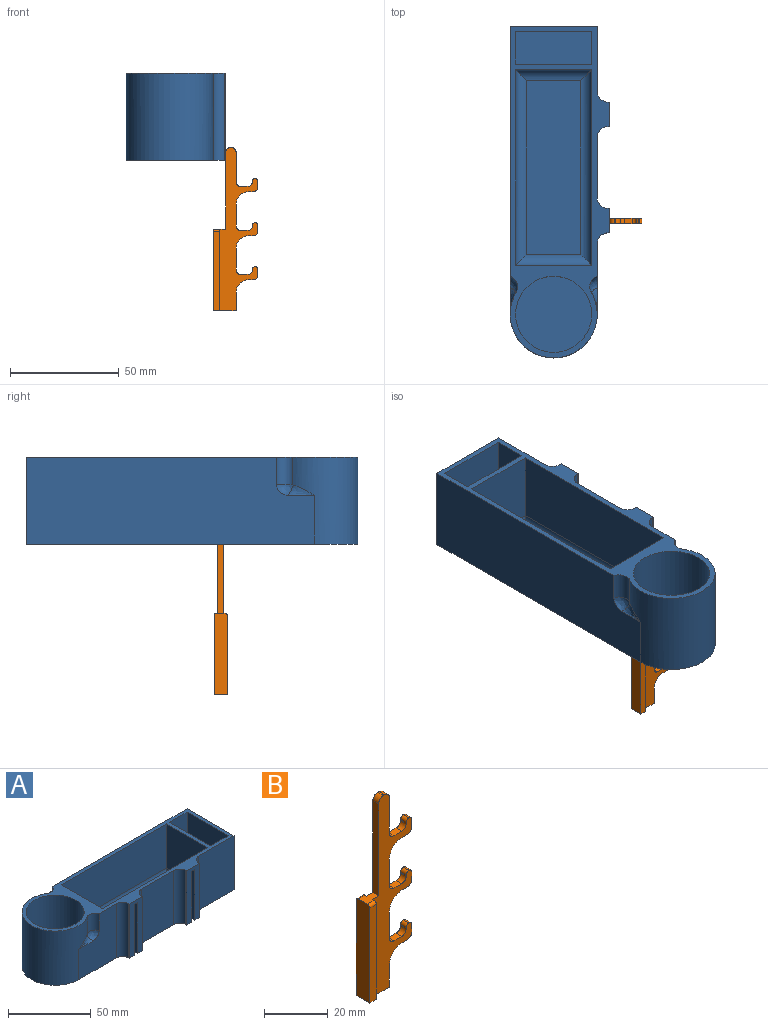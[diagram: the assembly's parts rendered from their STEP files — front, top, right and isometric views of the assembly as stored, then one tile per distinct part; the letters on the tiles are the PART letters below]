
ASSEMBLY  parts=2 mates=1
PART A: 56 faces, bbox 152.5x45.7x40 mm
  f0: plane 37.5x15mm, normal (0,1,0), area 562.5mm2, adj f1,f3,f4,f6
  f1: plane 37.5x35mm, normal (1,0,0), area 1312.5mm2, adj f0,f2,f4,f6
  f2: plane 37.5x15mm, normal (0,-1,0), area 562.5mm2, adj f1,f3,f4,f6
  f3: plane 37.5x35mm, normal (-1,0,0), area 1312.5mm2, adj f0,f2,f4,f6
  f4: plane 35x15mm, normal (0,0,1), area 525mm2, adj f0,f1,f2,f3
  f5: plane 6.2x5.7mm, normal (0,0,-1), area 26.6mm2, adj f9,f10,f11,f12,f13,f14,f15,f32
  f6: plane 152.5x45.7mm, normal (0,0,1), area 1382.2mm2, adj f0,f1,f2,f3,f23,f24,f25,f26
  f7: plane 6.2x5.7mm, normal (0,0,-1), area 26.6mm2, adj f16,f17,f18,f19,f20,f21,f22,f28
  f8: plane 152.5x45.7mm, normal (0,0,-1), area 6025mm2, adj f9,f10,f11,f12,f13,f14,f15,f16
  f9: plane 37.5x1.75mm, normal (0,1,0), area 65.6mm2, adj f5,f8,f10,f15
  f10: plane 37.5x3.2mm, normal (1,0,0), area 120mm2, adj f5,f8,f9,f11
  f11: plane 37.5x6.2mm, normal (0,-1,0), area 232.5mm2, adj f5,f8,f10,f12
  f12: plane 37.5x3.2mm, normal (-1,0,0), area 120mm2, adj f5,f8,f11,f13
  f13: plane 37.5x1.75mm, normal (0,1,0), area 65.6mm2, adj f5,f8,f12,f14
  f14: plane 37.5x2.5mm, normal (-1,0,0), area 93.8mm2, adj f5,f8,f13,f32
  f15: plane 37.5x2.5mm, normal (1,0,0), area 93.8mm2, adj f5,f8,f9,f32
  f16: plane 37.5x1.75mm, normal (0,1,0), area 65.6mm2, adj f7,f8,f17,f22
  f17: plane 37.5x3.2mm, normal (1,0,0), area 120mm2, adj f7,f8,f16,f18
  f18: plane 37.5x6.2mm, normal (0,-1,0), area 232.5mm2, adj f7,f8,f17,f19
  f19: plane 37.5x3.2mm, normal (-1,0,0), area 120mm2, adj f7,f8,f18,f20
  f20: plane 37.5x1.75mm, normal (0,1,0), area 65.6mm2, adj f7,f8,f19,f21
  f21: plane 37.5x2.5mm, normal (-1,0,0), area 93.8mm2, adj f7,f8,f20,f28
  f22: plane 37.5x2.5mm, normal (1,0,0), area 93.8mm2, adj f7,f8,f16,f28
  f23: cylinder r=20mm len=40mm, axis (0,0,1), area 2827.1mm2, adj f6,f8,f24,f34,f42,f43,f44,f45
  f24: plane 132.5x40mm, normal (0,1,0), area 4999.3mm2, adj f6,f8,f23,f25,f45,f46,f47
  f25: plane 40x40mm, normal (1,0,0), area 1600mm2, adj f6,f8,f24,f26
  f26: plane 40x29.89mm, normal (0,-1,0), area 1195.6mm2, adj f6,f8,f25,f48
  f27: plane 40x0.62mm, normal (1,0,0), area 24.8mm2, adj f6,f8,f28,f48
  f28: plane 40x11.2mm, normal (0,-1,0), area 346.8mm2, adj f6,f7,f8,f21,f22,f27,f29
  f29: plane 40x0.62mm, normal (-1,0,0), area 24.8mm2, adj f6,f8,f28,f51
  f30: plane 40x27.5mm, normal (0,-1,0), area 1100mm2, adj f6,f8,f50,f51
  f31: plane 40x0.62mm, normal (1,0,0), area 24.8mm2, adj f6,f8,f32,f50
  f32: plane 40x11.2mm, normal (0,-1,0), area 346.8mm2, adj f5,f6,f8,f14,f15,f31,f33
  f33: plane 40x0.62mm, normal (-1,0,0), area 24.8mm2, adj f6,f8,f32,f49
  f34: plane 40x32.39mm, normal (0,-1,0), area 994.9mm2, adj f6,f8,f23,f42,f43,f44,f49
  f35: plane 79.84x24.84mm, normal (0,0,1), area 1983.2mm2, adj f52,f53,f54,f55
  f36: plane 35x32.42mm, normal (1,0,0), area 1134.7mm2, adj f6,f37,f39,f54
  f37: plane 90x32.42mm, normal (0,1,0), area 2917.8mm2, adj f6,f36,f38,f55
  f38: plane 35x32.42mm, normal (-1,0,0), area 1134.7mm2, adj f6,f37,f39,f53
  f39: plane 90x32.42mm, normal (0,-1,0), area 2917.8mm2, adj f6,f36,f38,f52
  f40: plane 35x35mm, normal (0,0,1), area 962.1mm2, adj f41
  f41: cylinder r=17.5mm len=37.5mm, axis (0,0,-1), area 4123.3mm2, adj f6,f40
  f42: bspline ~13.08x4.89mm, area 33.2mm2, adj f23,f34,f43
  f43: bspline ~7.62x6.66mm, area 40.3mm2, adj f23,f34,f42,f44
  f44: cylinder r=5.08mm len=12.42mm, axis (0,0,1), area 111.9mm2, adj f6,f23,f34,f43
  f45: bspline ~13.08x4.89mm, area 33.7mm2, adj f23,f24,f46
  f46: bspline ~7.8x6.34mm, area 40.3mm2, adj f23,f24,f45,f47
  f47: cylinder r=5.08mm len=12.42mm, axis (0,0,1), area 111.9mm2, adj f6,f23,f24,f46
  f48: cylinder r=5.08mm len=40mm, axis (0,0,1), area 319.2mm2, adj f6,f8,f26,f27
  f49: cylinder r=5.08mm len=40mm, axis (0,0,1), area 319.2mm2, adj f6,f8,f33,f34
  f50: cylinder r=5.08mm len=40mm, axis (0,0,1), area 319.2mm2, adj f6,f8,f30,f31
  f51: cylinder r=5.08mm len=40mm, axis (0,0,-1), area 319.2mm2, adj f6,f8,f29,f30
  f52: cylinder r=5.08mm len=90mm, axis (1,0,0), area 688.7mm2, adj f35,f39,f53,f54
  f53: cylinder r=5.08mm len=35mm, axis (0,-1,0), area 249.8mm2, adj f35,f38,f52,f55
  f54: cylinder r=5.08mm len=35mm, axis (0,1,0), area 249.8mm2, adj f35,f36,f52,f55
  f55: cylinder r=5.08mm len=90mm, axis (-1,0,0), area 688.7mm2, adj f35,f37,f53,f54
PART B: 52 faces, bbox 20.5x6x75 mm
  f0: plane 2.5x0.51mm, normal (0,0,1), area 1.3mm2, adj f21,f22,f50,f51
  f1: plane 10.05x2.5mm, normal (1,0,0), area 25.1mm2, adj f21,f22,f25,f38
  f2: plane 2.5x2.3mm, normal (0,0,-1), area 5.7mm2, adj f21,f22,f27,f38
  f3: plane 2.84x2.5mm, normal (1,0,0), area 7.1mm2, adj f21,f22,f27,f33
  f4: plane 2.5x0.17mm, normal (0,0,1), area 0.4mm2, adj f21,f22,f32,f33
  f5: plane 2.5x0.34mm, normal (-1,0,0), area 0.8mm2, adj f21,f22,f26,f32
  f6: plane 3.5x2.5mm, normal (0,0,1), area 8.8mm2, adj f21,f22,f23,f26
  f7: plane 13.6x2.5mm, normal (1,0,0), area 34mm2, adj f21,f22,f23,f51
  f8: plane 10.5x6mm, normal (0,0,-1), area 36.8mm2, adj f9,f21,f22,f41,f42,f43,f44,f45
  f9: plane 8.55x2.5mm, normal (1,0,0), area 21.4mm2, adj f8,f21,f22,f39
  f10: plane 2.5x2.3mm, normal (0,0,-1), area 5.7mm2, adj f21,f22,f31,f39
  f11: plane 2.84x2.5mm, normal (1,0,0), area 7.1mm2, adj f21,f22,f31,f37
  f12: plane 2.5x0.17mm, normal (0,0,1), area 0.4mm2, adj f21,f22,f36,f37
  f13: plane 2.5x0.34mm, normal (-1,0,0), area 0.8mm2, adj f21,f22,f30,f36
  f14: plane 3.5x2.5mm, normal (0,0,1), area 8.8mm2, adj f21,f22,f24,f30
  f15: plane 10.05x2.5mm, normal (1,0,0), area 25.1mm2, adj f21,f22,f24,f40
  f16: plane 2.5x2.3mm, normal (0,0,-1), area 5.7mm2, adj f21,f22,f29,f40
  f17: plane 2.84x2.5mm, normal (1,0,0), area 7.1mm2, adj f21,f22,f29,f35
  f18: plane 2.5x0.17mm, normal (0,0,1), area 0.4mm2, adj f21,f22,f34,f35
  f19: plane 2.5x0.34mm, normal (-1,0,0), area 0.8mm2, adj f21,f22,f28,f34
  f20: plane 3.5x2.5mm, normal (0,0,1), area 8.8mm2, adj f21,f22,f25,f28
  f21: plane 75x17.5mm, normal (0,-1,0), area 582.3mm2, adj f0,f1,f2,f3,f4,f5,f6,f7
  f22: plane 75x17.5mm, normal (0,1,0), area 582.3mm2, adj f0,f1,f2,f3,f4,f5,f6,f7
  f23: cylinder r=2mm len=2.5mm, axis (0,1,0), area 7.9mm2, adj f6,f7,f21,f22
  f24: cylinder r=2mm len=2.5mm, axis (0,1,0), area 7.9mm2, adj f14,f15,f21,f22
  f25: cylinder r=2mm len=2.5mm, axis (0,1,0), area 7.9mm2, adj f1,f20,f21,f22
  f26: cylinder r=2mm len=2.5mm, axis (0,1,0), area 7.9mm2, adj f5,f6,f21,f22
  f27: cylinder r=2mm len=2.5mm, axis (0,1,0), area 7.9mm2, adj f2,f3,f21,f22
  f28: cylinder r=2mm len=2.5mm, axis (0,1,0), area 7.9mm2, adj f19,f20,f21,f22
  f29: cylinder r=2mm len=2.5mm, axis (0,1,0), area 7.9mm2, adj f16,f17,f21,f22
  f30: cylinder r=2mm len=2.5mm, axis (0,1,0), area 7.9mm2, adj f13,f14,f21,f22
  f31: cylinder r=2mm len=2.5mm, axis (0,1,0), area 7.9mm2, adj f10,f11,f21,f22
  f32: cylinder r=1.17mm len=2.5mm, axis (0,-1,0), area 4.6mm2, adj f4,f5,f21,f22
  f33: cylinder r=1.17mm len=2.5mm, axis (0,-1,0), area 4.6mm2, adj f3,f4,f21,f22
  f34: cylinder r=1.17mm len=2.5mm, axis (0,-1,0), area 4.6mm2, adj f18,f19,f21,f22
  f35: cylinder r=1.17mm len=2.5mm, axis (0,-1,0), area 4.6mm2, adj f17,f18,f21,f22
  f36: cylinder r=1.17mm len=2.5mm, axis (0,-1,0), area 4.6mm2, adj f12,f13,f21,f22
  f37: cylinder r=1.17mm len=2.5mm, axis (0,-1,0), area 4.6mm2, adj f11,f12,f21,f22
  f38: cylinder r=5.7mm len=5.7mm, axis (0,-1,0), area 22.4mm2, adj f1,f2,f21,f22
  f39: cylinder r=5.7mm len=5.7mm, axis (0,-1,0), area 22.4mm2, adj f9,f10,f21,f22
  f40: cylinder r=5.7mm len=5.7mm, axis (0,-1,0), area 22.4mm2, adj f15,f16,f21,f22
  f41: plane 37.5x1.75mm, normal (1,0,0), area 65.4mm2, adj f8,f22,f42,f46,f48
  f42: plane 36.5x3mm, normal (0,1,0), area 109.5mm2, adj f8,f41,f43,f48
  f43: plane 37.5x6mm, normal (-1,0,0), area 224.6mm2, adj f8,f42,f44,f46,f47,f48
  f44: plane 36.5x3mm, normal (0,-1,0), area 109.5mm2, adj f8,f43,f45,f47
  f45: plane 37.5x1.75mm, normal (1,0,0), area 65.4mm2, adj f8,f21,f44,f46,f47
  f46: plane 5.7x4mm, normal (0,0,1), area 18.8mm2, adj f21,f22,f41,f43,f45,f47,f48,f49
  f47: cylinder r=1mm len=3mm, axis (-1,0,0), area 4.7mm2, adj f43,f44,f45,f46
  f48: cylinder r=1mm len=3mm, axis (1,0,0), area 4.7mm2, adj f41,f42,f43,f46
  f49: plane 35.35x2.5mm, normal (-1,0,0), area 88.4mm2, adj f21,f22,f46,f50
  f50: cylinder r=2.15mm len=2.5mm, axis (0,-1,0), area 8.4mm2, adj f0,f21,f22,f49
  f51: cylinder r=2.15mm len=2.5mm, axis (0,-1,0), area 8.4mm2, adj f0,f7,f21,f22
PLACE A rot(axis=(0,0,1),90deg) t=(-70.42,5.87,-4.22)mm fixed
PLACE B t=(-47.42,-17.31,-75.98)mm
MATE planar A.f11 <-> B.f43  axis (1,0,0) through (-50.42,-18.56,12.03)mm
